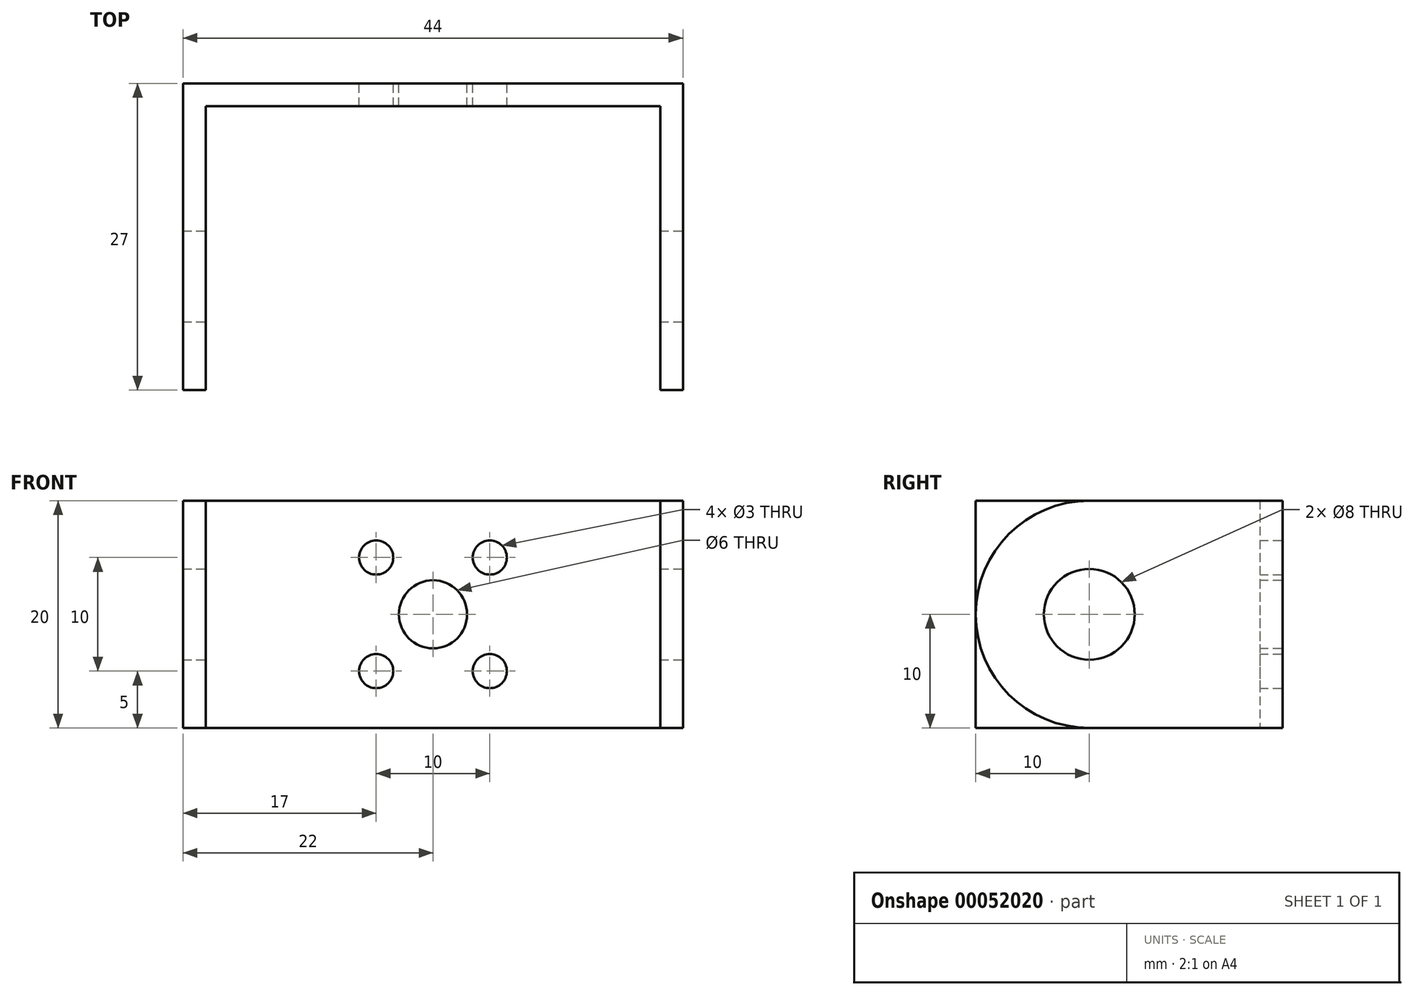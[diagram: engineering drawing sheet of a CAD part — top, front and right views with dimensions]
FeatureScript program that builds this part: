
annotation { "Feature Type Name" : "Feature", "Feature Type Description" : "" }
export const myFeature = defineFeature(function(context is Context, id is Id, definition is map)
    precondition{}
    {
        {
            var Q0;
            Q0=qCreatedBy(makeId("Top.planeOp"),FACE);
            var sketch = newSketch(context, id + "F0", { "sketchPlane" : qUnion([Q0])});
            skLineSegment(sketch, "E0.bottom", {"start": v(-22, -13.5) * mm, "end": v(-20, -13.5) * mm});
            skLineSegment(sketch, "E0.top", {"start": v(-22, 11.5) * mm, "end": v(-20, 11.5) * mm});
            skLineSegment(sketch, "E0.left", {"start": v(-22, -13.5) * mm, "end": v(-22, 11.5) * mm});
            skLineSegment(sketch, "E0.right", {"start": v(-20, -13.5) * mm, "end": v(-20, 11.5) * mm});
            skLineSegment(sketch, "E1.bottom", {"start": v(-22, 11.5) * mm, "end": v(22, 11.5) * mm});
            skLineSegment(sketch, "E1.top", {"start": v(-22, 13.5) * mm, "end": v(22, 13.5) * mm});
            skLineSegment(sketch, "E1.left", {"start": v(-22, 11.5) * mm, "end": v(-22, 13.5) * mm});
            skLineSegment(sketch, "E1.right", {"start": v(22, 11.5) * mm, "end": v(22, 13.5) * mm});
            skLineSegment(sketch, "E2.bottom", {"start": v(22, 11.5) * mm, "end": v(20, 11.5) * mm});
            skLineSegment(sketch, "E2.top", {"start": v(22, -13.5) * mm, "end": v(20, -13.5) * mm});
            skLineSegment(sketch, "E2.left", {"start": v(22, 11.5) * mm, "end": v(22, -13.5) * mm});
            skLineSegment(sketch, "E2.right", {"start": v(20, 11.5) * mm, "end": v(20, -13.5) * mm});
            skSolve(sketch);
        }
        {
            var Q0;
            Q0 = qSketchRegion(id + "F0", true);
            extrude(context, id + "F1", {"entities" : qUnion([Q0]), "endBound" : BoundingType.SYMMETRIC, "depth" : 20 * mm});
        }
        {
            var Q0;
            Q0=makeQuery(id+"F1.opExtrude","CAP_EDGE",EDGE,{"disambiguationData":[OSD([sQuery(id+"F0.wireOp",EDGE,"E2.top")])],"isStart":false});
            var Q1;
            Q1=makeQuery(id+"F1.opExtrude","CAP_EDGE",EDGE,{"disambiguationData":[OSD([sQuery(id+"F0.wireOp",EDGE,"E2.top")])],"isStart":true});
            fillet(context, id + "F2", {"entities" : qUnion([Q0, Q1]), "radius" : 10 * mm, "tangentPropagation" : true, "allowEdgeOverflow" : false});
        }
        {
            var Q0;
            Q0=makeQuery(id+"F1.opExtrude","SWEPT_FACE",FACE,{"disambiguationData":[OSD([sQuery(id+"F0.wireOp",EDGE,"E1.top")])]});
            var sketch = newSketch(context, id + "F3", { "sketchPlane" : qUnion([Q0])});
            skPoint(sketch, "E3", {"position": v(0, 0) * mm});
            skSolve(sketch);
        }
        {
            var Q0;
            Q0=sQuery(id+"F3.wireOp",VERTEX,"E3");
            var Q1;
            Q1=makeQuery(id+"F1.opExtrude","SWEPT_BODY",BODY,{"disambiguationData":[OSD([sQuery(id+"F0.wireOp",EDGE,"E0.bottom"),sQuery(id+"F0.wireOp",EDGE,"E0.left"),sQuery(id+"F0.wireOp",EDGE,"E0.right"),sQuery(id+"F0.wireOp",EDGE,"E1.bottom"),sQuery(id+"F0.wireOp",EDGE,"E1.top"),sQuery(id+"F0.wireOp",EDGE,"E1.left"),sQuery(id+"F0.wireOp",EDGE,"E1.right"),sQuery(id+"F0.wireOp",EDGE,"E2.top"),sQuery(id+"F0.wireOp",EDGE,"E2.left"),sQuery(id+"F0.wireOp",EDGE,"E2.right")])]});
            hole(context, id + "F4", {"style" : HoleStyle.SIMPLE, "holeDiameter" : 6 * mm, "endStyle" : HoleEndStyle.THROUGH, "locations" : qUnion([Q0]), "scope" : qUnion([Q1])});
        }
        {
            var Q0;
            Q0=makeQuery(id+"F1.opExtrude","SWEPT_FACE",FACE,{"disambiguationData":[OSD([sQuery(id+"F0.wireOp",EDGE,"E1.top")])]});
            var sketch = newSketch(context, id + "F5", { "sketchPlane" : qUnion([Q0])});
            skLineSegment(sketch, "E4.bottom", {"start": v(-5, 5) * mm, "end": v(5, 5) * mm});
            skLineSegment(sketch, "E4.top", {"start": v(-5, -5) * mm, "end": v(5, -5) * mm});
            skLineSegment(sketch, "E4.left", {"start": v(-5, 5) * mm, "end": v(-5, -5) * mm});
            skLineSegment(sketch, "E4.right", {"start": v(5, 5) * mm, "end": v(5, -5) * mm});
            skLineSegment(sketch, "E5", {"start": v(5, -5) * mm, "end": v(-5, 5) * mm});
            skPoint(sketch, "E6", {"position": v(0, 0) * mm});
            skSolve(sketch);
        }
        {
            var Q0;
            Q0=sQuery(id+"F5.wireOp",VERTEX,"E5.end");
            var Q1;
            Q1=sQuery(id+"F5.wireOp",VERTEX,"E4.right.start");
            var Q2;
            Q2=sQuery(id+"F5.wireOp",VERTEX,"E5.start");
            var Q3;
            Q3=sQuery(id+"F5.wireOp",VERTEX,"E4.left.end");
            var Q4;
            Q4=makeQuery(id+"F1.opExtrude","SWEPT_BODY",BODY,{"disambiguationData":[OSD([sQuery(id+"F0.wireOp",EDGE,"E0.bottom"),sQuery(id+"F0.wireOp",EDGE,"E0.left"),sQuery(id+"F0.wireOp",EDGE,"E0.right"),sQuery(id+"F0.wireOp",EDGE,"E1.bottom"),sQuery(id+"F0.wireOp",EDGE,"E1.top"),sQuery(id+"F0.wireOp",EDGE,"E1.left"),sQuery(id+"F0.wireOp",EDGE,"E1.right"),sQuery(id+"F0.wireOp",EDGE,"E2.top"),sQuery(id+"F0.wireOp",EDGE,"E2.left"),sQuery(id+"F0.wireOp",EDGE,"E2.right")])]});
            hole(context, id + "F6", {"style" : HoleStyle.SIMPLE, "holeDiameter" : 3 * mm, "endStyle" : HoleEndStyle.THROUGH, "locations" : qUnion([Q0, Q1, Q2, Q3]), "scope" : qUnion([Q4])});
        }
        {
            var Q0;
            Q0=makeQuery(id+"F1.opExtrude","SWEPT_FACE",FACE,{"disambiguationData":[OSD([sQuery(id+"F0.wireOp",EDGE,"E1.right"),sQuery(id+"F0.wireOp",EDGE,"E2.left")])]});
            var sketch = newSketch(context, id + "F7", { "sketchPlane" : qUnion([Q0])});
            skCircle(sketch, "E7", {"center": v(-3.5, 0) * mm, "radius": 3.18 * mm});
            skSolve(sketch);
        }
        {
            var Q0;
            Q0=sQuery(id+"F7.wireOp",VERTEX,"E7.center");
            var Q1;
            Q1=makeQuery(id+"F1.opExtrude","SWEPT_BODY",BODY,{"disambiguationData":[OSD([sQuery(id+"F0.wireOp",EDGE,"E0.bottom"),sQuery(id+"F0.wireOp",EDGE,"E0.left"),sQuery(id+"F0.wireOp",EDGE,"E0.right"),sQuery(id+"F0.wireOp",EDGE,"E1.bottom"),sQuery(id+"F0.wireOp",EDGE,"E1.top"),sQuery(id+"F0.wireOp",EDGE,"E1.left"),sQuery(id+"F0.wireOp",EDGE,"E1.right"),sQuery(id+"F0.wireOp",EDGE,"E2.top"),sQuery(id+"F0.wireOp",EDGE,"E2.left"),sQuery(id+"F0.wireOp",EDGE,"E2.right")])]});
            hole(context, id + "F8", {"style" : HoleStyle.SIMPLE, "holeDiameter" : 8 * mm, "endStyle" : HoleEndStyle.THROUGH, "locations" : qUnion([Q0]), "scope" : qUnion([Q1])});
        }
    });
